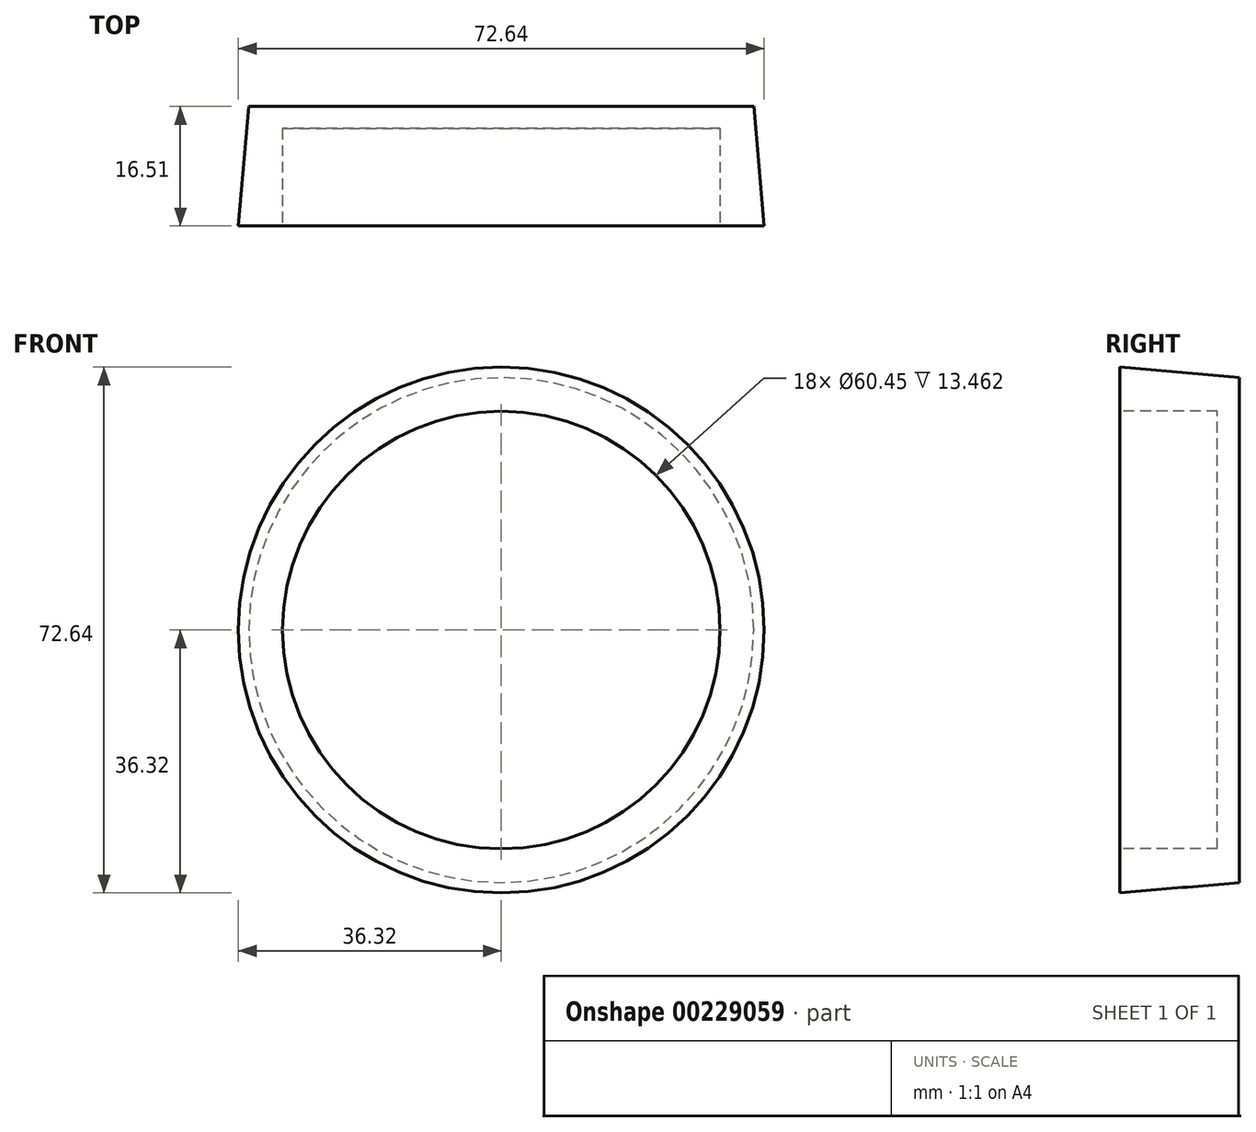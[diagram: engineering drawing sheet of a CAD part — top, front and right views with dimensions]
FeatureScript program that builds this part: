
annotation { "Feature Type Name" : "Feature", "Feature Type Description" : "" }
export const myFeature = defineFeature(function(context is Context, id is Id, definition is map)
    precondition{}
    {
        {
            var Q0;
            Q0=qCreatedBy(makeId("Front.planeOp"),FACE);
            var sketch = newSketch(context, id + "F0", { "sketchPlane" : qUnion([Q0])});
            skCircle(sketch, "E0", {"center": v(0, 0) * mm, "radius": 34.87 * mm});
            skSolve(sketch);
        }
        {
            var Q0;
            Q0 = qSketchRegion(id + "F0", true);
            extrude(context, id + "F1", {"entities" : qUnion([Q0]), "depth" : 16.5 * mm, "hasDraft" : true, "draftAngle" : 5 * degree});
        }
        {
            var Q0;
            Q0=makeQuery(id+"F1.opExtrude","CAP_FACE",FACE,{"disambiguationData":[OSD([sQuery(id+"F0.wireOp",EDGE,"E0")])],"isStart":false});
            var sketch = newSketch(context, id + "F2", { "sketchPlane" : qUnion([Q0])});
            skCircle(sketch, "E1", {"center": v(0, 0) * mm, "radius": 30.23 * mm});
            skSolve(sketch);
        }
        {
            var Q0;
            Q0 = qSketchRegion(id + "F2", true);
            extrude(context, id + "F3", {"entities" : qUnion([Q0]), "operationType" : NewBodyOperationType.REMOVE, "oppositeDirection" : true, "depth" : 13.46 * mm});
        }
    });
